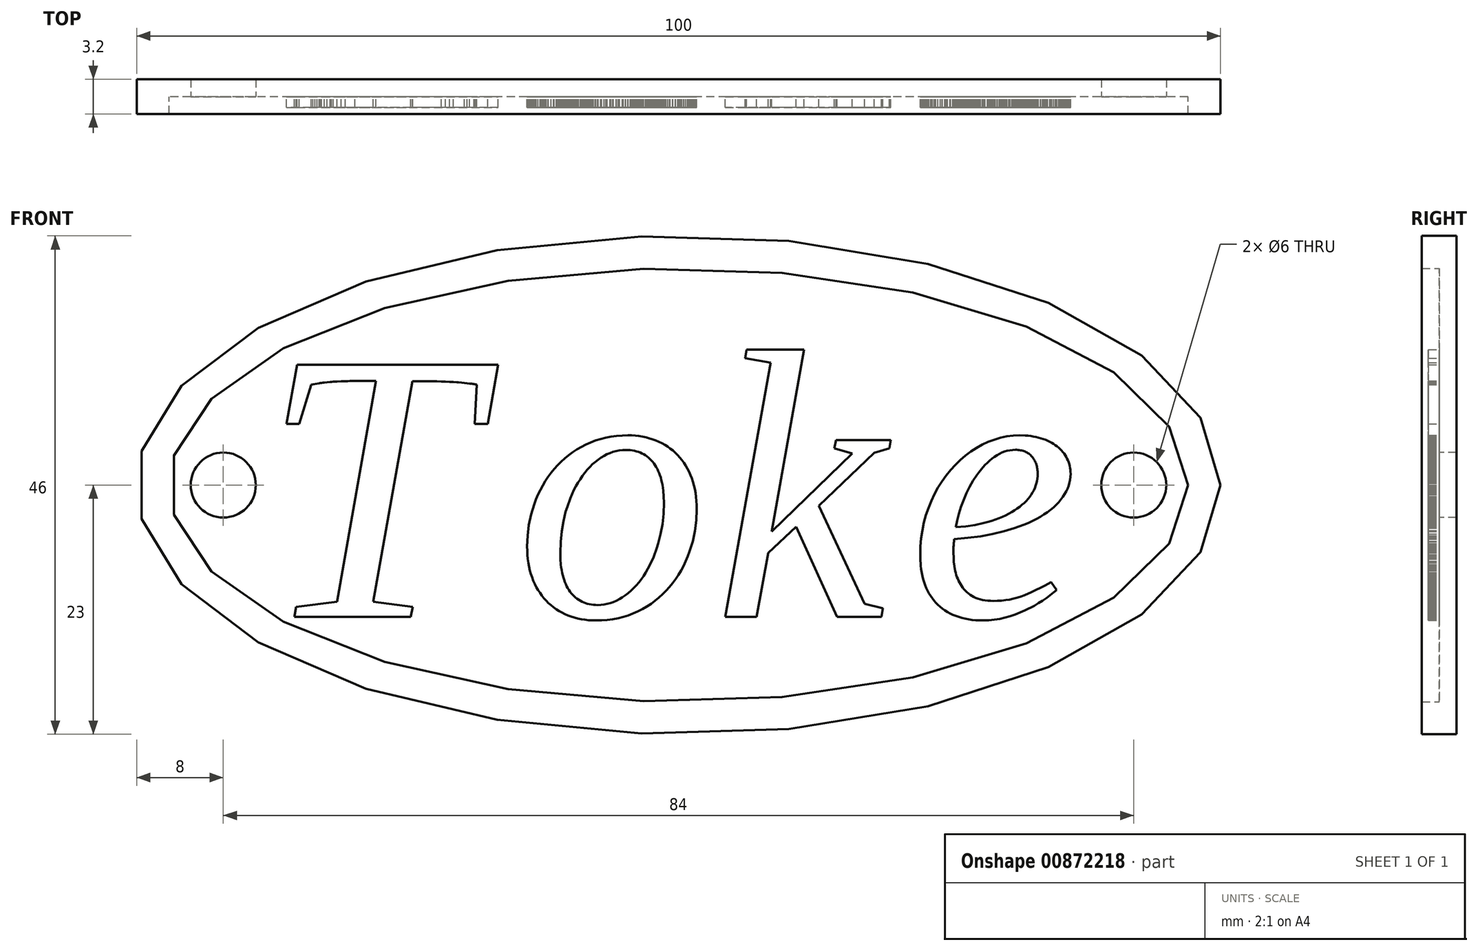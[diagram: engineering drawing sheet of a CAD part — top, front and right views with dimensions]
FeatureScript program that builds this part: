
annotation { "Feature Type Name" : "Feature", "Feature Type Description" : "" }
export const myFeature = defineFeature(function(context is Context, id is Id, definition is map)
    precondition{}
    {
        {
            var Q0;
            Q0=qCreatedBy(makeId("Front.planeOp"),FACE);
            var sketch = newSketch(context, id + "F0", { "sketchPlane" : qUnion([Q0])});
            skEllipse(sketch, "E0", {"center": v(0, 0) * mm, "majorRadius": 47 * mm, "minorRadius": 20 * mm, "majorAxis": v(1, 0)});
            skEllipse(sketch, "E1", {"center": v(0, 0) * mm, "majorRadius": 50 * mm, "minorRadius": 23 * mm, "majorAxis": v(1, 0)});
            skLineSegment(sketch, "E2", {"start": v(-81.12, 0) * mm, "end": v(85, 0) * mm, "construction": true});
            skPoint(sketch, "E2.startSnap0", {"position": v(-50, 0) * mm});
            skPoint(sketch, "E2.endSnap0", {"position": v(50, 0) * mm});
            skCircle(sketch, "E3", {"center": v(-42, 0) * mm, "radius": 3 * mm});
            skCircle(sketch, "E4", {"center": v(42, 0) * mm, "radius": 3 * mm});
            skLineSegment(sketch, "E5", {"start": v(-35.45, -12.15) * mm, "end": v(-35.27, -11.23) * mm});
            skLineSegment(sketch, "E6", {"start": v(-35.27, -11.23) * mm, "end": v(-31.5, -10.77) * mm});
            skLineSegment(sketch, "E7", {"start": v(-31.5, -10.77) * mm, "end": v(-27.92, 9.62) * mm});
            skLineSegment(sketch, "E8", {"start": v(-27.92, 9.62) * mm, "end": v(-28.8, 9.62) * mm});
            skLineSegment(sketch, "E9", {"start": v(-28.8, 9.62) * mm, "end": v(-29.35, 9.62) * mm});
            skLineSegment(sketch, "E10", {"start": v(-29.35, 9.62) * mm, "end": v(-29.85, 9.61) * mm});
            skLineSegment(sketch, "E11", {"start": v(-29.85, 9.61) * mm, "end": v(-30.32, 9.6) * mm});
            skLineSegment(sketch, "E12", {"start": v(-30.32, 9.6) * mm, "end": v(-30.54, 9.6) * mm});
            skLineSegment(sketch, "E13", {"start": v(-30.54, 9.6) * mm, "end": v(-30.74, 9.59) * mm});
            skLineSegment(sketch, "E14", {"start": v(-30.74, 9.59) * mm, "end": v(-31.14, 9.57) * mm});
            skLineSegment(sketch, "E15", {"start": v(-31.14, 9.57) * mm, "end": v(-31.5, 9.56) * mm});
            skLineSegment(sketch, "E16", {"start": v(-31.5, 9.56) * mm, "end": v(-31.84, 9.54) * mm});
            skLineSegment(sketch, "E17", {"start": v(-31.84, 9.54) * mm, "end": v(-32, 9.53) * mm});
            skLineSegment(sketch, "E18", {"start": v(-32, 9.53) * mm, "end": v(-32.15, 9.52) * mm});
            skLineSegment(sketch, "E19", {"start": v(-32.15, 9.52) * mm, "end": v(-32.43, 9.49) * mm});
            skLineSegment(sketch, "E20", {"start": v(-32.43, 9.49) * mm, "end": v(-32.7, 9.46) * mm});
            skLineSegment(sketch, "E21", {"start": v(-32.7, 9.46) * mm, "end": v(-32.82, 9.44) * mm});
            skLineSegment(sketch, "E22", {"start": v(-32.82, 9.44) * mm, "end": v(-32.94, 9.43) * mm});
            skLineSegment(sketch, "E23", {"start": v(-32.94, 9.43) * mm, "end": v(-33.05, 9.41) * mm});
            skLineSegment(sketch, "E24", {"start": v(-33.05, 9.41) * mm, "end": v(-33.16, 9.4) * mm});
            skLineSegment(sketch, "E25", {"start": v(-33.16, 9.4) * mm, "end": v(-33.36, 9.37) * mm});
            skLineSegment(sketch, "E26", {"start": v(-33.36, 9.37) * mm, "end": v(-33.55, 9.34) * mm});
            skLineSegment(sketch, "E27", {"start": v(-33.55, 9.34) * mm, "end": v(-33.73, 9.3) * mm});
            skLineSegment(sketch, "E28", {"start": v(-33.73, 9.3) * mm, "end": v(-33.9, 9.27) * mm});
            skLineSegment(sketch, "E29", {"start": v(-33.9, 9.27) * mm, "end": v(-35.01, 5.65) * mm});
            skLineSegment(sketch, "E30", {"start": v(-35.01, 5.65) * mm, "end": v(-36.17, 5.65) * mm});
            skLineSegment(sketch, "E31", {"start": v(-36.17, 5.65) * mm, "end": v(-35.2, 11.11) * mm});
            skLineSegment(sketch, "E32", {"start": v(-35.2, 11.11) * mm, "end": v(-16.64, 11.11) * mm});
            skLineSegment(sketch, "E33", {"start": v(-16.64, 11.11) * mm, "end": v(-17.61, 5.65) * mm});
            skLineSegment(sketch, "E34", {"start": v(-17.61, 5.65) * mm, "end": v(-18.8, 5.65) * mm});
            skLineSegment(sketch, "E35", {"start": v(-18.8, 5.65) * mm, "end": v(-18.62, 9.27) * mm});
            skLineSegment(sketch, "E36", {"start": v(-18.62, 9.27) * mm, "end": v(-18.7, 9.29) * mm});
            skLineSegment(sketch, "E37", {"start": v(-18.7, 9.29) * mm, "end": v(-18.78, 9.3) * mm});
            skLineSegment(sketch, "E38", {"start": v(-18.78, 9.3) * mm, "end": v(-18.87, 9.32) * mm});
            skLineSegment(sketch, "E39", {"start": v(-18.87, 9.32) * mm, "end": v(-18.96, 9.33) * mm});
            skLineSegment(sketch, "E40", {"start": v(-18.96, 9.33) * mm, "end": v(-19.06, 9.35) * mm});
            skLineSegment(sketch, "E41", {"start": v(-19.06, 9.35) * mm, "end": v(-19.16, 9.36) * mm});
            skLineSegment(sketch, "E42", {"start": v(-19.16, 9.36) * mm, "end": v(-19.27, 9.37) * mm});
            skLineSegment(sketch, "E43", {"start": v(-19.27, 9.37) * mm, "end": v(-19.5, 9.4) * mm});
            skLineSegment(sketch, "E44", {"start": v(-19.5, 9.4) * mm, "end": v(-19.75, 9.42) * mm});
            skLineSegment(sketch, "E45", {"start": v(-19.75, 9.42) * mm, "end": v(-20.02, 9.45) * mm});
            skLineSegment(sketch, "E46", {"start": v(-20.02, 9.45) * mm, "end": v(-20.3, 9.47) * mm});
            skLineSegment(sketch, "E47", {"start": v(-20.3, 9.47) * mm, "end": v(-20.46, 9.48) * mm});
            skLineSegment(sketch, "E48", {"start": v(-20.46, 9.48) * mm, "end": v(-20.78, 9.5) * mm});
            skLineSegment(sketch, "E49", {"start": v(-20.78, 9.5) * mm, "end": v(-21.12, 9.53) * mm});
            skLineSegment(sketch, "E50", {"start": v(-21.12, 9.53) * mm, "end": v(-21.5, 9.54) * mm});
            skLineSegment(sketch, "E51", {"start": v(-21.5, 9.54) * mm, "end": v(-21.89, 9.56) * mm});
            skLineSegment(sketch, "E52", {"start": v(-21.89, 9.56) * mm, "end": v(-22.3, 9.57) * mm});
            skLineSegment(sketch, "E53", {"start": v(-22.3, 9.57) * mm, "end": v(-22.75, 9.58) * mm});
            skLineSegment(sketch, "E54", {"start": v(-22.75, 9.58) * mm, "end": v(-23.22, 9.58) * mm});
            skLineSegment(sketch, "E55", {"start": v(-23.22, 9.58) * mm, "end": v(-23.72, 9.59) * mm});
            skLineSegment(sketch, "E56", {"start": v(-23.72, 9.59) * mm, "end": v(-24.57, 9.59) * mm});
            skLineSegment(sketch, "E57", {"start": v(-24.57, 9.59) * mm, "end": v(-28.16, -10.77) * mm});
            skLineSegment(sketch, "E58", {"start": v(-28.16, -10.77) * mm, "end": v(-24.53, -11.23) * mm});
            skLineSegment(sketch, "E59", {"start": v(-24.53, -11.23) * mm, "end": v(-24.7, -12.15) * mm});
            skLineSegment(sketch, "E60", {"start": v(-24.7, -12.15) * mm, "end": v(-35.45, -12.15) * mm});
            skLineSegment(sketch, "E61", {"start": v(-10.91, -6.25) * mm, "end": v(-10.9, -6.82) * mm});
            skLineSegment(sketch, "E62", {"start": v(-10.9, -6.82) * mm, "end": v(-10.86, -7.36) * mm});
            skLineSegment(sketch, "E63", {"start": v(-10.86, -7.36) * mm, "end": v(-10.82, -7.61) * mm});
            skLineSegment(sketch, "E64", {"start": v(-10.82, -7.61) * mm, "end": v(-10.79, -7.86) * mm});
            skLineSegment(sketch, "E65", {"start": v(-10.79, -7.86) * mm, "end": v(-10.74, -8.1) * mm});
            skLineSegment(sketch, "E66", {"start": v(-10.74, -8.1) * mm, "end": v(-10.69, -8.32) * mm});
            skLineSegment(sketch, "E67", {"start": v(-10.69, -8.32) * mm, "end": v(-10.63, -8.54) * mm});
            skLineSegment(sketch, "E68", {"start": v(-10.63, -8.54) * mm, "end": v(-10.56, -8.76) * mm});
            skLineSegment(sketch, "E69", {"start": v(-10.56, -8.76) * mm, "end": v(-10.49, -8.96) * mm});
            skLineSegment(sketch, "E70", {"start": v(-10.49, -8.96) * mm, "end": v(-10.4, -9.15) * mm});
            skLineSegment(sketch, "E71", {"start": v(-10.4, -9.15) * mm, "end": v(-10.32, -9.34) * mm});
            skLineSegment(sketch, "E72", {"start": v(-10.32, -9.34) * mm, "end": v(-10.22, -9.52) * mm});
            skLineSegment(sketch, "E73", {"start": v(-10.22, -9.52) * mm, "end": v(-10.12, -9.69) * mm});
            skLineSegment(sketch, "E74", {"start": v(-10.12, -9.69) * mm, "end": v(-10.01, -9.85) * mm});
            skLineSegment(sketch, "E75", {"start": v(-10.01, -9.85) * mm, "end": v(-9.9, -10) * mm});
            skLineSegment(sketch, "E76", {"start": v(-9.9, -10) * mm, "end": v(-9.77, -10.13) * mm});
            skLineSegment(sketch, "E77", {"start": v(-9.77, -10.13) * mm, "end": v(-9.64, -10.26) * mm});
            skLineSegment(sketch, "E78", {"start": v(-9.64, -10.26) * mm, "end": v(-9.5, -10.38) * mm});
            skLineSegment(sketch, "E79", {"start": v(-9.5, -10.38) * mm, "end": v(-9.37, -10.5) * mm});
            skLineSegment(sketch, "E80", {"start": v(-9.37, -10.5) * mm, "end": v(-9.22, -10.6) * mm});
            skLineSegment(sketch, "E81", {"start": v(-9.22, -10.6) * mm, "end": v(-9.07, -10.69) * mm});
            skLineSegment(sketch, "E82", {"start": v(-9.07, -10.69) * mm, "end": v(-8.91, -10.77) * mm});
            skLineSegment(sketch, "E83", {"start": v(-8.91, -10.77) * mm, "end": v(-8.75, -10.84) * mm});
            skLineSegment(sketch, "E84", {"start": v(-8.75, -10.84) * mm, "end": v(-8.58, -10.9) * mm});
            skLineSegment(sketch, "E85", {"start": v(-8.58, -10.9) * mm, "end": v(-8.41, -10.96) * mm});
            skLineSegment(sketch, "E86", {"start": v(-8.41, -10.96) * mm, "end": v(-8.23, -11) * mm});
            skLineSegment(sketch, "E87", {"start": v(-8.23, -11) * mm, "end": v(-8.05, -11.03) * mm});
            skLineSegment(sketch, "E88", {"start": v(-8.05, -11.03) * mm, "end": v(-7.86, -11.06) * mm});
            skLineSegment(sketch, "E89", {"start": v(-7.86, -11.06) * mm, "end": v(-7.66, -11.07) * mm});
            skLineSegment(sketch, "E90", {"start": v(-7.66, -11.07) * mm, "end": v(-7.46, -11.08) * mm});
            skLineSegment(sketch, "E91", {"start": v(-7.46, -11.08) * mm, "end": v(-7.16, -11.07) * mm});
            skLineSegment(sketch, "E92", {"start": v(-7.16, -11.07) * mm, "end": v(-6.87, -11.03) * mm});
            skLineSegment(sketch, "E93", {"start": v(-6.87, -11.03) * mm, "end": v(-6.58, -10.98) * mm});
            skLineSegment(sketch, "E94", {"start": v(-6.58, -10.98) * mm, "end": v(-6.29, -10.9) * mm});
            skLineSegment(sketch, "E95", {"start": v(-6.29, -10.9) * mm, "end": v(-6, -10.8) * mm});
            skLineSegment(sketch, "E96", {"start": v(-6, -10.8) * mm, "end": v(-5.72, -10.68) * mm});
            skLineSegment(sketch, "E97", {"start": v(-5.72, -10.68) * mm, "end": v(-5.45, -10.53) * mm});
            skLineSegment(sketch, "E98", {"start": v(-5.45, -10.53) * mm, "end": v(-5.17, -10.37) * mm});
            skLineSegment(sketch, "E99", {"start": v(-5.17, -10.37) * mm, "end": v(-4.9, -10.18) * mm});
            skLineSegment(sketch, "E100", {"start": v(-4.9, -10.18) * mm, "end": v(-4.63, -9.97) * mm});
            skLineSegment(sketch, "E101", {"start": v(-4.63, -9.97) * mm, "end": v(-4.38, -9.75) * mm});
            skLineSegment(sketch, "E102", {"start": v(-4.38, -9.75) * mm, "end": v(-4.13, -9.5) * mm});
            skLineSegment(sketch, "E103", {"start": v(-4.13, -9.5) * mm, "end": v(-3.9, -9.25) * mm});
            skLineSegment(sketch, "E104", {"start": v(-3.9, -9.25) * mm, "end": v(-3.66, -8.98) * mm});
            skLineSegment(sketch, "E105", {"start": v(-3.66, -8.98) * mm, "end": v(-3.44, -8.7) * mm});
            skLineSegment(sketch, "E106", {"start": v(-3.44, -8.7) * mm, "end": v(-3.23, -8.39) * mm});
            skLineSegment(sketch, "E107", {"start": v(-3.23, -8.39) * mm, "end": v(-3.02, -8.06) * mm});
            skLineSegment(sketch, "E108", {"start": v(-3.02, -8.06) * mm, "end": v(-2.82, -7.73) * mm});
            skLineSegment(sketch, "E109", {"start": v(-2.82, -7.73) * mm, "end": v(-2.64, -7.38) * mm});
            skLineSegment(sketch, "E110", {"start": v(-2.64, -7.38) * mm, "end": v(-2.3, -6.63) * mm});
            skLineSegment(sketch, "E111", {"start": v(-2.3, -6.63) * mm, "end": v(-2, -5.83) * mm});
            skLineSegment(sketch, "E112", {"start": v(-2, -5.83) * mm, "end": v(-1.87, -5.4) * mm});
            skLineSegment(sketch, "E113", {"start": v(-1.87, -5.4) * mm, "end": v(-1.65, -4.52) * mm});
            skLineSegment(sketch, "E114", {"start": v(-1.65, -4.52) * mm, "end": v(-1.48, -3.6) * mm});
            skLineSegment(sketch, "E115", {"start": v(-1.48, -3.6) * mm, "end": v(-1.39, -2.64) * mm});
            skLineSegment(sketch, "E116", {"start": v(-1.39, -2.64) * mm, "end": v(-1.35, -1.64) * mm});
            skLineSegment(sketch, "E117", {"start": v(-1.35, -1.64) * mm, "end": v(-1.37, -1.06) * mm});
            skLineSegment(sketch, "E118", {"start": v(-1.37, -1.06) * mm, "end": v(-1.41, -0.52) * mm});
            skLineSegment(sketch, "E119", {"start": v(-1.41, -0.52) * mm, "end": v(-1.44, -0.26) * mm});
            skLineSegment(sketch, "E120", {"start": v(-1.44, -0.26) * mm, "end": v(-1.48, 0) * mm});
            skLineSegment(sketch, "E121", {"start": v(-1.48, 0) * mm, "end": v(-1.53, 0.23) * mm});
            skLineSegment(sketch, "E122", {"start": v(-1.53, 0.23) * mm, "end": v(-1.58, 0.46) * mm});
            skLineSegment(sketch, "E123", {"start": v(-1.58, 0.46) * mm, "end": v(-1.64, 0.69) * mm});
            skLineSegment(sketch, "E124", {"start": v(-1.64, 0.69) * mm, "end": v(-1.71, 0.9) * mm});
            skLineSegment(sketch, "E125", {"start": v(-1.71, 0.9) * mm, "end": v(-1.79, 1.1) * mm});
            skLineSegment(sketch, "E126", {"start": v(-1.79, 1.1) * mm, "end": v(-1.87, 1.3) * mm});
            skLineSegment(sketch, "E127", {"start": v(-1.87, 1.3) * mm, "end": v(-1.96, 1.48) * mm});
            skLineSegment(sketch, "E128", {"start": v(-1.96, 1.48) * mm, "end": v(-2.06, 1.66) * mm});
            skLineSegment(sketch, "E129", {"start": v(-2.06, 1.66) * mm, "end": v(-2.16, 1.83) * mm});
            skLineSegment(sketch, "E130", {"start": v(-2.16, 1.83) * mm, "end": v(-2.27, 1.99) * mm});
            skLineSegment(sketch, "E131", {"start": v(-2.27, 1.99) * mm, "end": v(-2.39, 2.14) * mm});
            skLineSegment(sketch, "E132", {"start": v(-2.39, 2.14) * mm, "end": v(-2.51, 2.28) * mm});
            skLineSegment(sketch, "E133", {"start": v(-2.51, 2.28) * mm, "end": v(-2.64, 2.41) * mm});
            skLineSegment(sketch, "E134", {"start": v(-2.64, 2.41) * mm, "end": v(-2.77, 2.53) * mm});
            skLineSegment(sketch, "E135", {"start": v(-2.77, 2.53) * mm, "end": v(-2.91, 2.65) * mm});
            skLineSegment(sketch, "E136", {"start": v(-2.91, 2.65) * mm, "end": v(-3.06, 2.75) * mm});
            skLineSegment(sketch, "E137", {"start": v(-3.06, 2.75) * mm, "end": v(-3.22, 2.84) * mm});
            skLineSegment(sketch, "E138", {"start": v(-3.22, 2.84) * mm, "end": v(-3.37, 2.92) * mm});
            skLineSegment(sketch, "E139", {"start": v(-3.37, 2.92) * mm, "end": v(-3.54, 3) * mm});
            skLineSegment(sketch, "E140", {"start": v(-3.54, 3) * mm, "end": v(-3.71, 3.06) * mm});
            skLineSegment(sketch, "E141", {"start": v(-3.71, 3.06) * mm, "end": v(-3.9, 3.11) * mm});
            skLineSegment(sketch, "E142", {"start": v(-3.9, 3.11) * mm, "end": v(-4.08, 3.16) * mm});
            skLineSegment(sketch, "E143", {"start": v(-4.08, 3.16) * mm, "end": v(-4.27, 3.2) * mm});
            skLineSegment(sketch, "E144", {"start": v(-4.27, 3.2) * mm, "end": v(-4.46, 3.22) * mm});
            skLineSegment(sketch, "E145", {"start": v(-4.46, 3.22) * mm, "end": v(-4.67, 3.23) * mm});
            skLineSegment(sketch, "E146", {"start": v(-4.67, 3.23) * mm, "end": v(-4.88, 3.24) * mm});
            skLineSegment(sketch, "E147", {"start": v(-4.88, 3.24) * mm, "end": v(-5.17, 3.22) * mm});
            skLineSegment(sketch, "E148", {"start": v(-5.17, 3.22) * mm, "end": v(-5.46, 3.2) * mm});
            skLineSegment(sketch, "E149", {"start": v(-5.46, 3.2) * mm, "end": v(-5.75, 3.14) * mm});
            skLineSegment(sketch, "E150", {"start": v(-5.75, 3.14) * mm, "end": v(-6.03, 3.06) * mm});
            skLineSegment(sketch, "E151", {"start": v(-6.03, 3.06) * mm, "end": v(-6.32, 2.96) * mm});
            skLineSegment(sketch, "E152", {"start": v(-6.32, 2.96) * mm, "end": v(-6.6, 2.84) * mm});
            skLineSegment(sketch, "E153", {"start": v(-6.6, 2.84) * mm, "end": v(-6.87, 2.7) * mm});
            skLineSegment(sketch, "E154", {"start": v(-6.87, 2.7) * mm, "end": v(-7.15, 2.52) * mm});
            skLineSegment(sketch, "E155", {"start": v(-7.15, 2.52) * mm, "end": v(-7.42, 2.34) * mm});
            skLineSegment(sketch, "E156", {"start": v(-7.42, 2.34) * mm, "end": v(-7.68, 2.13) * mm});
            skLineSegment(sketch, "E157", {"start": v(-7.68, 2.13) * mm, "end": v(-7.93, 1.91) * mm});
            skLineSegment(sketch, "E158", {"start": v(-7.93, 1.91) * mm, "end": v(-8.18, 1.67) * mm});
            skLineSegment(sketch, "E159", {"start": v(-8.18, 1.67) * mm, "end": v(-8.41, 1.42) * mm});
            skLineSegment(sketch, "E160", {"start": v(-8.41, 1.42) * mm, "end": v(-8.64, 1.15) * mm});
            skLineSegment(sketch, "E161", {"start": v(-8.64, 1.15) * mm, "end": v(-8.86, 0.85) * mm});
            skLineSegment(sketch, "E162", {"start": v(-8.86, 0.85) * mm, "end": v(-9.07, 0.55) * mm});
            skLineSegment(sketch, "E163", {"start": v(-9.07, 0.55) * mm, "end": v(-9.28, 0.23) * mm});
            skLineSegment(sketch, "E164", {"start": v(-9.28, 0.23) * mm, "end": v(-9.47, -0.1) * mm});
            skLineSegment(sketch, "E165", {"start": v(-9.47, -0.1) * mm, "end": v(-9.65, -0.46) * mm});
            skLineSegment(sketch, "E166", {"start": v(-9.65, -0.46) * mm, "end": v(-9.82, -0.83) * mm});
            skLineSegment(sketch, "E167", {"start": v(-9.82, -0.83) * mm, "end": v(-9.99, -1.21) * mm});
            skLineSegment(sketch, "E168", {"start": v(-9.99, -1.21) * mm, "end": v(-10.28, -2.02) * mm});
            skLineSegment(sketch, "E169", {"start": v(-10.28, -2.02) * mm, "end": v(-10.4, -2.45) * mm});
            skLineSegment(sketch, "E170", {"start": v(-10.4, -2.45) * mm, "end": v(-10.63, -3.34) * mm});
            skLineSegment(sketch, "E171", {"start": v(-10.63, -3.34) * mm, "end": v(-10.79, -4.27) * mm});
            skLineSegment(sketch, "E172", {"start": v(-10.79, -4.27) * mm, "end": v(-10.88, -5.24) * mm});
            skLineSegment(sketch, "E173", {"start": v(-10.88, -5.24) * mm, "end": v(-10.91, -6.25) * mm});
            skLineSegment(sketch, "E174", {"start": v(-7.62, -12.5) * mm, "end": v(-7.96, -12.5) * mm});
            skLineSegment(sketch, "E175", {"start": v(-7.96, -12.5) * mm, "end": v(-8.3, -12.47) * mm});
            skLineSegment(sketch, "E176", {"start": v(-8.3, -12.47) * mm, "end": v(-8.64, -12.43) * mm});
            skLineSegment(sketch, "E177", {"start": v(-8.64, -12.43) * mm, "end": v(-8.97, -12.38) * mm});
            skLineSegment(sketch, "E178", {"start": v(-8.97, -12.38) * mm, "end": v(-9.29, -12.32) * mm});
            skLineSegment(sketch, "E179", {"start": v(-9.29, -12.32) * mm, "end": v(-9.6, -12.24) * mm});
            skLineSegment(sketch, "E180", {"start": v(-9.6, -12.24) * mm, "end": v(-9.9, -12.14) * mm});
            skLineSegment(sketch, "E181", {"start": v(-9.9, -12.14) * mm, "end": v(-10.2, -12.03) * mm});
            skLineSegment(sketch, "E182", {"start": v(-10.2, -12.03) * mm, "end": v(-10.49, -11.9) * mm});
            skLineSegment(sketch, "E183", {"start": v(-10.49, -11.9) * mm, "end": v(-10.76, -11.77) * mm});
            skLineSegment(sketch, "E184", {"start": v(-10.76, -11.77) * mm, "end": v(-11.03, -11.62) * mm});
            skLineSegment(sketch, "E185", {"start": v(-11.03, -11.62) * mm, "end": v(-11.29, -11.46) * mm});
            skLineSegment(sketch, "E186", {"start": v(-11.29, -11.46) * mm, "end": v(-11.53, -11.28) * mm});
            skLineSegment(sketch, "E187", {"start": v(-11.53, -11.28) * mm, "end": v(-11.77, -11.1) * mm});
            skLineSegment(sketch, "E188", {"start": v(-11.77, -11.1) * mm, "end": v(-12, -10.9) * mm});
            skLineSegment(sketch, "E189", {"start": v(-12, -10.9) * mm, "end": v(-12.21, -10.68) * mm});
            skLineSegment(sketch, "E190", {"start": v(-12.21, -10.68) * mm, "end": v(-12.42, -10.45) * mm});
            skLineSegment(sketch, "E191", {"start": v(-12.42, -10.45) * mm, "end": v(-12.6, -10.21) * mm});
            skLineSegment(sketch, "E192", {"start": v(-12.6, -10.21) * mm, "end": v(-12.79, -9.96) * mm});
            skLineSegment(sketch, "E193", {"start": v(-12.79, -9.96) * mm, "end": v(-12.96, -9.7) * mm});
            skLineSegment(sketch, "E194", {"start": v(-12.96, -9.7) * mm, "end": v(-13.11, -9.42) * mm});
            skLineSegment(sketch, "E195", {"start": v(-13.11, -9.42) * mm, "end": v(-13.26, -9.14) * mm});
            skLineSegment(sketch, "E196", {"start": v(-13.26, -9.14) * mm, "end": v(-13.4, -8.84) * mm});
            skLineSegment(sketch, "E197", {"start": v(-13.4, -8.84) * mm, "end": v(-13.52, -8.53) * mm});
            skLineSegment(sketch, "E198", {"start": v(-13.52, -8.53) * mm, "end": v(-13.62, -8.2) * mm});
            skLineSegment(sketch, "E199", {"start": v(-13.62, -8.2) * mm, "end": v(-13.71, -7.87) * mm});
            skLineSegment(sketch, "E200", {"start": v(-13.71, -7.87) * mm, "end": v(-13.8, -7.53) * mm});
            skLineSegment(sketch, "E201", {"start": v(-13.8, -7.53) * mm, "end": v(-13.85, -7.18) * mm});
            skLineSegment(sketch, "E202", {"start": v(-13.85, -7.18) * mm, "end": v(-13.9, -6.82) * mm});
            skLineSegment(sketch, "E203", {"start": v(-13.9, -6.82) * mm, "end": v(-13.94, -6.44) * mm});
            skLineSegment(sketch, "E204", {"start": v(-13.94, -6.44) * mm, "end": v(-13.96, -6.06) * mm});
            skLineSegment(sketch, "E205", {"start": v(-13.96, -6.06) * mm, "end": v(-13.97, -5.66) * mm});
            skLineSegment(sketch, "E206", {"start": v(-13.97, -5.66) * mm, "end": v(-13.93, -4.66) * mm});
            skLineSegment(sketch, "E207", {"start": v(-13.93, -4.66) * mm, "end": v(-13.8, -3.68) * mm});
            skLineSegment(sketch, "E208", {"start": v(-13.8, -3.68) * mm, "end": v(-13.6, -2.72) * mm});
            skLineSegment(sketch, "E209", {"start": v(-13.6, -2.72) * mm, "end": v(-13.32, -1.78) * mm});
            skLineSegment(sketch, "E210", {"start": v(-13.32, -1.78) * mm, "end": v(-13.15, -1.32) * mm});
            skLineSegment(sketch, "E211", {"start": v(-13.15, -1.32) * mm, "end": v(-12.96, -0.88) * mm});
            skLineSegment(sketch, "E212", {"start": v(-12.96, -0.88) * mm, "end": v(-12.75, -0.45) * mm});
            skLineSegment(sketch, "E213", {"start": v(-12.75, -0.45) * mm, "end": v(-12.53, -0.03) * mm});
            skLineSegment(sketch, "E214", {"start": v(-12.53, -0.03) * mm, "end": v(-12.3, 0.37) * mm});
            skLineSegment(sketch, "E215", {"start": v(-12.3, 0.37) * mm, "end": v(-12.03, 0.75) * mm});
            skLineSegment(sketch, "E216", {"start": v(-12.03, 0.75) * mm, "end": v(-11.76, 1.13) * mm});
            skLineSegment(sketch, "E217", {"start": v(-11.76, 1.13) * mm, "end": v(-11.47, 1.48) * mm});
            skLineSegment(sketch, "E218", {"start": v(-11.47, 1.48) * mm, "end": v(-11.16, 1.83) * mm});
            skLineSegment(sketch, "E219", {"start": v(-11.16, 1.83) * mm, "end": v(-10.83, 2.16) * mm});
            skLineSegment(sketch, "E220", {"start": v(-10.83, 2.16) * mm, "end": v(-10.49, 2.47) * mm});
            skLineSegment(sketch, "E221", {"start": v(-10.49, 2.47) * mm, "end": v(-10.13, 2.76) * mm});
            skLineSegment(sketch, "E222", {"start": v(-10.13, 2.76) * mm, "end": v(-9.75, 3.03) * mm});
            skLineSegment(sketch, "E223", {"start": v(-9.75, 3.03) * mm, "end": v(-9.36, 3.29) * mm});
            skLineSegment(sketch, "E224", {"start": v(-9.36, 3.29) * mm, "end": v(-8.96, 3.52) * mm});
            skLineSegment(sketch, "E225", {"start": v(-8.96, 3.52) * mm, "end": v(-8.54, 3.74) * mm});
            skLineSegment(sketch, "E226", {"start": v(-8.54, 3.74) * mm, "end": v(-8.1, 3.94) * mm});
            skLineSegment(sketch, "E227", {"start": v(-8.1, 3.94) * mm, "end": v(-7.65, 4.11) * mm});
            skLineSegment(sketch, "E228", {"start": v(-7.65, 4.11) * mm, "end": v(-7.19, 4.26) * mm});
            skLineSegment(sketch, "E229", {"start": v(-7.19, 4.26) * mm, "end": v(-6.71, 4.38) * mm});
            skLineSegment(sketch, "E230", {"start": v(-6.71, 4.38) * mm, "end": v(-6.22, 4.47) * mm});
            skLineSegment(sketch, "E231", {"start": v(-6.22, 4.47) * mm, "end": v(-5.72, 4.54) * mm});
            skLineSegment(sketch, "E232", {"start": v(-5.72, 4.54) * mm, "end": v(-5.2, 4.58) * mm});
            skLineSegment(sketch, "E233", {"start": v(-5.2, 4.58) * mm, "end": v(-4.67, 4.59) * mm});
            skLineSegment(sketch, "E234", {"start": v(-4.67, 4.59) * mm, "end": v(-4.32, 4.58) * mm});
            skLineSegment(sketch, "E235", {"start": v(-4.32, 4.58) * mm, "end": v(-3.98, 4.56) * mm});
            skLineSegment(sketch, "E236", {"start": v(-3.98, 4.56) * mm, "end": v(-3.65, 4.52) * mm});
            skLineSegment(sketch, "E237", {"start": v(-3.65, 4.52) * mm, "end": v(-3.32, 4.47) * mm});
            skLineSegment(sketch, "E238", {"start": v(-3.32, 4.47) * mm, "end": v(-3, 4.4) * mm});
            skLineSegment(sketch, "E239", {"start": v(-3, 4.4) * mm, "end": v(-2.7, 4.33) * mm});
            skLineSegment(sketch, "E240", {"start": v(-2.7, 4.33) * mm, "end": v(-2.4, 4.23) * mm});
            skLineSegment(sketch, "E241", {"start": v(-2.4, 4.23) * mm, "end": v(-2.1, 4.12) * mm});
            skLineSegment(sketch, "E242", {"start": v(-2.1, 4.12) * mm, "end": v(-1.81, 4) * mm});
            skLineSegment(sketch, "E243", {"start": v(-1.81, 4) * mm, "end": v(-1.53, 3.86) * mm});
            skLineSegment(sketch, "E244", {"start": v(-1.53, 3.86) * mm, "end": v(-1.26, 3.71) * mm});
            skLineSegment(sketch, "E245", {"start": v(-1.26, 3.71) * mm, "end": v(-1, 3.55) * mm});
            skLineSegment(sketch, "E246", {"start": v(-1, 3.55) * mm, "end": v(-0.76, 3.37) * mm});
            skLineSegment(sketch, "E247", {"start": v(-0.76, 3.37) * mm, "end": v(-0.53, 3.18) * mm});
            skLineSegment(sketch, "E248", {"start": v(-0.53, 3.18) * mm, "end": v(-0.3, 2.98) * mm});
            skLineSegment(sketch, "E249", {"start": v(-0.3, 2.98) * mm, "end": v(-0.09, 2.77) * mm});
            skLineSegment(sketch, "E250", {"start": v(-0.09, 2.77) * mm, "end": v(0.12, 2.54) * mm});
            skLineSegment(sketch, "E251", {"start": v(0.12, 2.54) * mm, "end": v(0.31, 2.3) * mm});
            skLineSegment(sketch, "E252", {"start": v(0.31, 2.3) * mm, "end": v(0.5, 2.05) * mm});
            skLineSegment(sketch, "E253", {"start": v(0.5, 2.05) * mm, "end": v(0.66, 1.79) * mm});
            skLineSegment(sketch, "E254", {"start": v(0.66, 1.79) * mm, "end": v(0.82, 1.51) * mm});
            skLineSegment(sketch, "E255", {"start": v(0.82, 1.51) * mm, "end": v(0.96, 1.23) * mm});
            skLineSegment(sketch, "E256", {"start": v(0.96, 1.23) * mm, "end": v(1.1, 0.93) * mm});
            skLineSegment(sketch, "E257", {"start": v(1.1, 0.93) * mm, "end": v(1.21, 0.62) * mm});
            skLineSegment(sketch, "E258", {"start": v(1.21, 0.62) * mm, "end": v(1.32, 0.3) * mm});
            skLineSegment(sketch, "E259", {"start": v(1.32, 0.3) * mm, "end": v(1.42, -0.04) * mm});
            skLineSegment(sketch, "E260", {"start": v(1.42, -0.04) * mm, "end": v(1.5, -0.38) * mm});
            skLineSegment(sketch, "E261", {"start": v(1.5, -0.38) * mm, "end": v(1.57, -0.73) * mm});
            skLineSegment(sketch, "E262", {"start": v(1.57, -0.73) * mm, "end": v(1.62, -1.1) * mm});
            skLineSegment(sketch, "E263", {"start": v(1.62, -1.1) * mm, "end": v(1.65, -1.47) * mm});
            skLineSegment(sketch, "E264", {"start": v(1.65, -1.47) * mm, "end": v(1.68, -1.85) * mm});
            skLineSegment(sketch, "E265", {"start": v(1.68, -1.85) * mm, "end": v(1.68, -2.25) * mm});
            skLineSegment(sketch, "E266", {"start": v(1.68, -2.25) * mm, "end": v(1.64, -3.25) * mm});
            skLineSegment(sketch, "E267", {"start": v(1.64, -3.25) * mm, "end": v(1.52, -4.23) * mm});
            skLineSegment(sketch, "E268", {"start": v(1.52, -4.23) * mm, "end": v(1.31, -5.2) * mm});
            skLineSegment(sketch, "E269", {"start": v(1.31, -5.2) * mm, "end": v(1.02, -6.13) * mm});
            skLineSegment(sketch, "E270", {"start": v(1.02, -6.13) * mm, "end": v(0.85, -6.6) * mm});
            skLineSegment(sketch, "E271", {"start": v(0.85, -6.6) * mm, "end": v(0.67, -7.03) * mm});
            skLineSegment(sketch, "E272", {"start": v(0.67, -7.03) * mm, "end": v(0.46, -7.46) * mm});
            skLineSegment(sketch, "E273", {"start": v(0.46, -7.46) * mm, "end": v(0.24, -7.88) * mm});
            skLineSegment(sketch, "E274", {"start": v(0.24, -7.88) * mm, "end": v(0, -8.28) * mm});
            skLineSegment(sketch, "E275", {"start": v(0, -8.28) * mm, "end": v(-0.26, -8.67) * mm});
            skLineSegment(sketch, "E276", {"start": v(-0.26, -8.67) * mm, "end": v(-0.54, -9.05) * mm});
            skLineSegment(sketch, "E277", {"start": v(-0.54, -9.05) * mm, "end": v(-0.83, -9.41) * mm});
            skLineSegment(sketch, "E278", {"start": v(-0.83, -9.41) * mm, "end": v(-1.14, -9.75) * mm});
            skLineSegment(sketch, "E279", {"start": v(-1.14, -9.75) * mm, "end": v(-1.46, -10.08) * mm});
            skLineSegment(sketch, "E280", {"start": v(-1.46, -10.08) * mm, "end": v(-1.8, -10.39) * mm});
            skLineSegment(sketch, "E281", {"start": v(-1.8, -10.39) * mm, "end": v(-2.16, -10.68) * mm});
            skLineSegment(sketch, "E282", {"start": v(-2.16, -10.68) * mm, "end": v(-2.53, -10.95) * mm});
            skLineSegment(sketch, "E283", {"start": v(-2.53, -10.95) * mm, "end": v(-2.92, -11.2) * mm});
            skLineSegment(sketch, "E284", {"start": v(-2.92, -11.2) * mm, "end": v(-3.33, -11.45) * mm});
            skLineSegment(sketch, "E285", {"start": v(-3.33, -11.45) * mm, "end": v(-3.75, -11.67) * mm});
            skLineSegment(sketch, "E286", {"start": v(-3.75, -11.67) * mm, "end": v(-4.18, -11.86) * mm});
            skLineSegment(sketch, "E287", {"start": v(-4.18, -11.86) * mm, "end": v(-4.63, -12.03) * mm});
            skLineSegment(sketch, "E288", {"start": v(-4.63, -12.03) * mm, "end": v(-5.1, -12.17) * mm});
            skLineSegment(sketch, "E289", {"start": v(-5.1, -12.17) * mm, "end": v(-5.57, -12.3) * mm});
            skLineSegment(sketch, "E290", {"start": v(-5.57, -12.3) * mm, "end": v(-6.06, -12.38) * mm});
            skLineSegment(sketch, "E291", {"start": v(-6.06, -12.38) * mm, "end": v(-6.57, -12.45) * mm});
            skLineSegment(sketch, "E292", {"start": v(-6.57, -12.45) * mm, "end": v(-7.09, -12.49) * mm});
            skLineSegment(sketch, "E293", {"start": v(-7.09, -12.49) * mm, "end": v(-7.62, -12.5) * mm});
            skLineSegment(sketch, "E294", {"start": v(8.48, 11.3) * mm, "end": v(6.14, 11.72) * mm});
            skLineSegment(sketch, "E295", {"start": v(6.14, 11.72) * mm, "end": v(6.28, 12.5) * mm});
            skLineSegment(sketch, "E296", {"start": v(6.28, 12.5) * mm, "end": v(11.57, 12.5) * mm});
            skLineSegment(sketch, "E297", {"start": v(11.57, 12.5) * mm, "end": v(8.59, -4.3) * mm});
            skLineSegment(sketch, "E298", {"start": v(8.59, -4.3) * mm, "end": v(16.01, 2.9) * mm});
            skLineSegment(sketch, "E299", {"start": v(16.01, 2.9) * mm, "end": v(14.38, 3.37) * mm});
            skLineSegment(sketch, "E300", {"start": v(14.38, 3.37) * mm, "end": v(14.52, 4.16) * mm});
            skLineSegment(sketch, "E301", {"start": v(14.52, 4.16) * mm, "end": v(19.59, 4.16) * mm});
            skLineSegment(sketch, "E302", {"start": v(19.59, 4.16) * mm, "end": v(19.45, 3.37) * mm});
            skLineSegment(sketch, "E303", {"start": v(19.45, 3.37) * mm, "end": v(18.04, 2.98) * mm});
            skLineSegment(sketch, "E304", {"start": v(18.04, 2.98) * mm, "end": v(12.94, -1.9) * mm});
            skLineSegment(sketch, "E305", {"start": v(12.94, -1.9) * mm, "end": v(17.16, -10.97) * mm});
            skLineSegment(sketch, "E306", {"start": v(17.16, -10.97) * mm, "end": v(18.86, -11.37) * mm});
            skLineSegment(sketch, "E307", {"start": v(18.86, -11.37) * mm, "end": v(18.72, -12.15) * mm});
            skLineSegment(sketch, "E308", {"start": v(18.72, -12.15) * mm, "end": v(14.63, -12.15) * mm});
            skLineSegment(sketch, "E309", {"start": v(14.63, -12.15) * mm, "end": v(10.84, -3.84) * mm});
            skLineSegment(sketch, "E310", {"start": v(10.84, -3.84) * mm, "end": v(8.28, -6.25) * mm});
            skLineSegment(sketch, "E311", {"start": v(8.28, -6.25) * mm, "end": v(7.2, -12.15) * mm});
            skLineSegment(sketch, "E312", {"start": v(7.2, -12.15) * mm, "end": v(4.32, -12.15) * mm});
            skLineSegment(sketch, "E313", {"start": v(4.32, -12.15) * mm, "end": v(8.48, 11.3) * mm});
            skLineSegment(sketch, "E314", {"start": v(36.17, 1.03) * mm, "end": v(36.16, 0.75) * mm});
            skLineSegment(sketch, "E315", {"start": v(36.16, 0.75) * mm, "end": v(36.13, 0.48) * mm});
            skLineSegment(sketch, "E316", {"start": v(36.13, 0.48) * mm, "end": v(36.07, 0.2) * mm});
            skLineSegment(sketch, "E317", {"start": v(36.07, 0.2) * mm, "end": v(36, -0.07) * mm});
            skLineSegment(sketch, "E318", {"start": v(36, -0.07) * mm, "end": v(35.9, -0.33) * mm});
            skLineSegment(sketch, "E319", {"start": v(35.9, -0.33) * mm, "end": v(35.77, -0.6) * mm});
            skLineSegment(sketch, "E320", {"start": v(35.77, -0.6) * mm, "end": v(35.63, -0.85) * mm});
            skLineSegment(sketch, "E321", {"start": v(35.63, -0.85) * mm, "end": v(35.46, -1.1) * mm});
            skLineSegment(sketch, "E322", {"start": v(35.46, -1.1) * mm, "end": v(35.27, -1.35) * mm});
            skLineSegment(sketch, "E323", {"start": v(35.27, -1.35) * mm, "end": v(35.07, -1.6) * mm});
            skLineSegment(sketch, "E324", {"start": v(35.07, -1.6) * mm, "end": v(34.84, -1.83) * mm});
            skLineSegment(sketch, "E325", {"start": v(34.84, -1.83) * mm, "end": v(34.59, -2.06) * mm});
            skLineSegment(sketch, "E326", {"start": v(34.59, -2.06) * mm, "end": v(34.32, -2.28) * mm});
            skLineSegment(sketch, "E327", {"start": v(34.32, -2.28) * mm, "end": v(34.02, -2.5) * mm});
            skLineSegment(sketch, "E328", {"start": v(34.02, -2.5) * mm, "end": v(33.71, -2.72) * mm});
            skLineSegment(sketch, "E329", {"start": v(33.71, -2.72) * mm, "end": v(33.38, -2.92) * mm});
            skLineSegment(sketch, "E330", {"start": v(33.38, -2.92) * mm, "end": v(33.03, -3.12) * mm});
            skLineSegment(sketch, "E331", {"start": v(33.03, -3.12) * mm, "end": v(32.66, -3.3) * mm});
            skLineSegment(sketch, "E332", {"start": v(32.66, -3.3) * mm, "end": v(32.27, -3.49) * mm});
            skLineSegment(sketch, "E333", {"start": v(32.27, -3.49) * mm, "end": v(31.86, -3.66) * mm});
            skLineSegment(sketch, "E334", {"start": v(31.86, -3.66) * mm, "end": v(31.43, -3.83) * mm});
            skLineSegment(sketch, "E335", {"start": v(31.43, -3.83) * mm, "end": v(30.98, -3.98) * mm});
            skLineSegment(sketch, "E336", {"start": v(30.98, -3.98) * mm, "end": v(30.02, -4.28) * mm});
            skLineSegment(sketch, "E337", {"start": v(30.02, -4.28) * mm, "end": v(28.98, -4.52) * mm});
            skLineSegment(sketch, "E338", {"start": v(28.98, -4.52) * mm, "end": v(27.87, -4.72) * mm});
            skLineSegment(sketch, "E339", {"start": v(27.87, -4.72) * mm, "end": v(26.7, -4.88) * mm});
            skLineSegment(sketch, "E340", {"start": v(26.7, -4.88) * mm, "end": v(25.44, -4.99) * mm});
            skLineSegment(sketch, "E341", {"start": v(25.44, -4.99) * mm, "end": v(25.43, -5) * mm});
            skLineSegment(sketch, "E342", {"start": v(25.43, -5) * mm, "end": v(25.43, -5.03) * mm});
            skLineSegment(sketch, "E343", {"start": v(25.43, -5.03) * mm, "end": v(25.43, -5.05) * mm});
            skLineSegment(sketch, "E344", {"start": v(25.43, -5.05) * mm, "end": v(25.43, -5.08) * mm});
            skLineSegment(sketch, "E345", {"start": v(25.43, -5.08) * mm, "end": v(25.42, -5.1) * mm});
            skLineSegment(sketch, "E346", {"start": v(25.42, -5.1) * mm, "end": v(25.42, -5.13) * mm});
            skLineSegment(sketch, "E347", {"start": v(25.42, -5.13) * mm, "end": v(25.42, -5.16) * mm});
            skLineSegment(sketch, "E348", {"start": v(25.42, -5.16) * mm, "end": v(25.41, -5.19) * mm});
            skLineSegment(sketch, "E349", {"start": v(25.41, -5.19) * mm, "end": v(25.4, -5.25) * mm});
            skLineSegment(sketch, "E350", {"start": v(25.4, -5.25) * mm, "end": v(25.4, -5.32) * mm});
            skLineSegment(sketch, "E351", {"start": v(25.4, -5.32) * mm, "end": v(25.4, -5.4) * mm});
            skLineSegment(sketch, "E352", {"start": v(25.4, -5.4) * mm, "end": v(25.38, -5.47) * mm});
            skLineSegment(sketch, "E353", {"start": v(25.38, -5.47) * mm, "end": v(25.38, -5.56) * mm});
            skLineSegment(sketch, "E354", {"start": v(25.38, -5.56) * mm, "end": v(25.37, -5.74) * mm});
            skLineSegment(sketch, "E355", {"start": v(25.37, -5.74) * mm, "end": v(25.37, -5.93) * mm});
            skLineSegment(sketch, "E356", {"start": v(25.37, -5.93) * mm, "end": v(25.37, -6.14) * mm});
            skLineSegment(sketch, "E357", {"start": v(25.37, -6.14) * mm, "end": v(25.37, -6.25) * mm});
            skLineSegment(sketch, "E358", {"start": v(25.37, -6.25) * mm, "end": v(25.38, -6.68) * mm});
            skLineSegment(sketch, "E359", {"start": v(25.38, -6.68) * mm, "end": v(25.4, -7.1) * mm});
            skLineSegment(sketch, "E360", {"start": v(25.4, -7.1) * mm, "end": v(25.45, -7.5) * mm});
            skLineSegment(sketch, "E361", {"start": v(25.45, -7.5) * mm, "end": v(25.52, -7.9) * mm});
            skLineSegment(sketch, "E362", {"start": v(25.52, -7.9) * mm, "end": v(25.57, -8.1) * mm});
            skLineSegment(sketch, "E363", {"start": v(25.57, -8.1) * mm, "end": v(25.62, -8.3) * mm});
            skLineSegment(sketch, "E364", {"start": v(25.62, -8.3) * mm, "end": v(25.69, -8.48) * mm});
            skLineSegment(sketch, "E365", {"start": v(25.69, -8.48) * mm, "end": v(25.76, -8.66) * mm});
            skLineSegment(sketch, "E366", {"start": v(25.76, -8.66) * mm, "end": v(25.83, -8.83) * mm});
            skLineSegment(sketch, "E367", {"start": v(25.83, -8.83) * mm, "end": v(25.92, -9) * mm});
            skLineSegment(sketch, "E368", {"start": v(25.92, -9) * mm, "end": v(26.01, -9.17) * mm});
            skLineSegment(sketch, "E369", {"start": v(26.01, -9.17) * mm, "end": v(26.11, -9.33) * mm});
            skLineSegment(sketch, "E370", {"start": v(26.11, -9.33) * mm, "end": v(26.22, -9.48) * mm});
            skLineSegment(sketch, "E371", {"start": v(26.22, -9.48) * mm, "end": v(26.34, -9.62) * mm});
            skLineSegment(sketch, "E372", {"start": v(26.34, -9.62) * mm, "end": v(26.47, -9.76) * mm});
            skLineSegment(sketch, "E373", {"start": v(26.47, -9.76) * mm, "end": v(26.6, -9.89) * mm});
            skLineSegment(sketch, "E374", {"start": v(26.6, -9.89) * mm, "end": v(26.75, -10.01) * mm});
            skLineSegment(sketch, "E375", {"start": v(26.75, -10.01) * mm, "end": v(26.9, -10.13) * mm});
            skLineSegment(sketch, "E376", {"start": v(26.9, -10.13) * mm, "end": v(27.07, -10.23) * mm});
            skLineSegment(sketch, "E377", {"start": v(27.07, -10.23) * mm, "end": v(27.24, -10.33) * mm});
            skLineSegment(sketch, "E378", {"start": v(27.24, -10.33) * mm, "end": v(27.42, -10.42) * mm});
            skLineSegment(sketch, "E379", {"start": v(27.42, -10.42) * mm, "end": v(27.62, -10.5) * mm});
            skLineSegment(sketch, "E380", {"start": v(27.62, -10.5) * mm, "end": v(27.83, -10.55) * mm});
            skLineSegment(sketch, "E381", {"start": v(27.83, -10.55) * mm, "end": v(28.05, -10.6) * mm});
            skLineSegment(sketch, "E382", {"start": v(28.05, -10.6) * mm, "end": v(28.28, -10.64) * mm});
            skLineSegment(sketch, "E383", {"start": v(28.28, -10.64) * mm, "end": v(28.52, -10.67) * mm});
            skLineSegment(sketch, "E384", {"start": v(28.52, -10.67) * mm, "end": v(28.78, -10.7) * mm});
            skLineSegment(sketch, "E385", {"start": v(28.78, -10.7) * mm, "end": v(29.04, -10.7) * mm});
            skLineSegment(sketch, "E386", {"start": v(29.04, -10.7) * mm, "end": v(29.43, -10.69) * mm});
            skLineSegment(sketch, "E387", {"start": v(29.43, -10.69) * mm, "end": v(29.8, -10.66) * mm});
            skLineSegment(sketch, "E388", {"start": v(29.8, -10.66) * mm, "end": v(30.18, -10.62) * mm});
            skLineSegment(sketch, "E389", {"start": v(30.18, -10.62) * mm, "end": v(30.54, -10.57) * mm});
            skLineSegment(sketch, "E390", {"start": v(30.54, -10.57) * mm, "end": v(30.9, -10.5) * mm});
            skLineSegment(sketch, "E391", {"start": v(30.9, -10.5) * mm, "end": v(31.25, -10.4) * mm});
            skLineSegment(sketch, "E392", {"start": v(31.25, -10.4) * mm, "end": v(31.6, -10.3) * mm});
            skLineSegment(sketch, "E393", {"start": v(31.6, -10.3) * mm, "end": v(31.92, -10.18) * mm});
            skLineSegment(sketch, "E394", {"start": v(31.92, -10.18) * mm, "end": v(32.57, -9.9) * mm});
            skLineSegment(sketch, "E395", {"start": v(32.57, -9.9) * mm, "end": v(33.8, -9.3) * mm});
            skLineSegment(sketch, "E396", {"start": v(33.8, -9.3) * mm, "end": v(34.39, -8.96) * mm});
            skLineSegment(sketch, "E397", {"start": v(34.39, -8.96) * mm, "end": v(34.9, -9.69) * mm});
            skLineSegment(sketch, "E398", {"start": v(34.9, -9.69) * mm, "end": v(34.6, -9.93) * mm});
            skLineSegment(sketch, "E399", {"start": v(34.6, -9.93) * mm, "end": v(34.29, -10.17) * mm});
            skLineSegment(sketch, "E400", {"start": v(34.29, -10.17) * mm, "end": v(33.95, -10.41) * mm});
            skLineSegment(sketch, "E401", {"start": v(33.95, -10.41) * mm, "end": v(33.59, -10.66) * mm});
            skLineSegment(sketch, "E402", {"start": v(33.59, -10.66) * mm, "end": v(33.2, -10.9) * mm});
            skLineSegment(sketch, "E403", {"start": v(33.2, -10.9) * mm, "end": v(32.8, -11.14) * mm});
            skLineSegment(sketch, "E404", {"start": v(32.8, -11.14) * mm, "end": v(31.96, -11.58) * mm});
            skLineSegment(sketch, "E405", {"start": v(31.96, -11.58) * mm, "end": v(31.52, -11.77) * mm});
            skLineSegment(sketch, "E406", {"start": v(31.52, -11.77) * mm, "end": v(31.06, -11.94) * mm});
            skLineSegment(sketch, "E407", {"start": v(31.06, -11.94) * mm, "end": v(30.6, -12.1) * mm});
            skLineSegment(sketch, "E408", {"start": v(30.6, -12.1) * mm, "end": v(30.12, -12.24) * mm});
            skLineSegment(sketch, "E409", {"start": v(30.12, -12.24) * mm, "end": v(29.63, -12.35) * mm});
            skLineSegment(sketch, "E410", {"start": v(29.63, -12.35) * mm, "end": v(29.14, -12.43) * mm});
            skLineSegment(sketch, "E411", {"start": v(29.14, -12.43) * mm, "end": v(28.64, -12.48) * mm});
            skLineSegment(sketch, "E412", {"start": v(28.64, -12.48) * mm, "end": v(28.14, -12.5) * mm});
            skLineSegment(sketch, "E413", {"start": v(28.14, -12.5) * mm, "end": v(27.78, -12.5) * mm});
            skLineSegment(sketch, "E414", {"start": v(27.78, -12.5) * mm, "end": v(27.43, -12.47) * mm});
            skLineSegment(sketch, "E415", {"start": v(27.43, -12.47) * mm, "end": v(27.09, -12.44) * mm});
            skLineSegment(sketch, "E416", {"start": v(27.09, -12.44) * mm, "end": v(26.76, -12.4) * mm});
            skLineSegment(sketch, "E417", {"start": v(26.76, -12.4) * mm, "end": v(26.45, -12.34) * mm});
            skLineSegment(sketch, "E418", {"start": v(26.45, -12.34) * mm, "end": v(26.14, -12.27) * mm});
            skLineSegment(sketch, "E419", {"start": v(26.14, -12.27) * mm, "end": v(25.85, -12.18) * mm});
            skLineSegment(sketch, "E420", {"start": v(25.85, -12.18) * mm, "end": v(25.57, -12.08) * mm});
            skLineSegment(sketch, "E421", {"start": v(25.57, -12.08) * mm, "end": v(25.3, -11.97) * mm});
            skLineSegment(sketch, "E422", {"start": v(25.3, -11.97) * mm, "end": v(25.05, -11.85) * mm});
            skLineSegment(sketch, "E423", {"start": v(25.05, -11.85) * mm, "end": v(24.8, -11.7) * mm});
            skLineSegment(sketch, "E424", {"start": v(24.8, -11.7) * mm, "end": v(24.57, -11.56) * mm});
            skLineSegment(sketch, "E425", {"start": v(24.57, -11.56) * mm, "end": v(24.35, -11.4) * mm});
            skLineSegment(sketch, "E426", {"start": v(24.35, -11.4) * mm, "end": v(24.14, -11.24) * mm});
            skLineSegment(sketch, "E427", {"start": v(24.14, -11.24) * mm, "end": v(23.94, -11.06) * mm});
            skLineSegment(sketch, "E428", {"start": v(23.94, -11.06) * mm, "end": v(23.75, -10.87) * mm});
            skLineSegment(sketch, "E429", {"start": v(23.75, -10.87) * mm, "end": v(23.58, -10.67) * mm});
            skLineSegment(sketch, "E430", {"start": v(23.58, -10.67) * mm, "end": v(23.41, -10.46) * mm});
            skLineSegment(sketch, "E431", {"start": v(23.41, -10.46) * mm, "end": v(23.26, -10.23) * mm});
            skLineSegment(sketch, "E432", {"start": v(23.26, -10.23) * mm, "end": v(23.11, -10) * mm});
            skLineSegment(sketch, "E433", {"start": v(23.11, -10) * mm, "end": v(22.98, -9.76) * mm});
            skLineSegment(sketch, "E434", {"start": v(22.98, -9.76) * mm, "end": v(22.86, -9.5) * mm});
            skLineSegment(sketch, "E435", {"start": v(22.86, -9.5) * mm, "end": v(22.76, -9.24) * mm});
            skLineSegment(sketch, "E436", {"start": v(22.76, -9.24) * mm, "end": v(22.66, -8.96) * mm});
            skLineSegment(sketch, "E437", {"start": v(22.66, -8.96) * mm, "end": v(22.57, -8.67) * mm});
            skLineSegment(sketch, "E438", {"start": v(22.57, -8.67) * mm, "end": v(22.5, -8.38) * mm});
            skLineSegment(sketch, "E439", {"start": v(22.5, -8.38) * mm, "end": v(22.44, -8.08) * mm});
            skLineSegment(sketch, "E440", {"start": v(22.44, -8.08) * mm, "end": v(22.39, -7.76) * mm});
            skLineSegment(sketch, "E441", {"start": v(22.39, -7.76) * mm, "end": v(22.35, -7.44) * mm});
            skLineSegment(sketch, "E442", {"start": v(22.35, -7.44) * mm, "end": v(22.3, -6.77) * mm});
            skLineSegment(sketch, "E443", {"start": v(22.3, -6.77) * mm, "end": v(22.3, -6.43) * mm});
            skLineSegment(sketch, "E444", {"start": v(22.3, -6.43) * mm, "end": v(22.32, -5.66) * mm});
            skLineSegment(sketch, "E445", {"start": v(22.32, -5.66) * mm, "end": v(22.38, -4.92) * mm});
            skLineSegment(sketch, "E446", {"start": v(22.38, -4.92) * mm, "end": v(22.5, -4.19) * mm});
            skLineSegment(sketch, "E447", {"start": v(22.5, -4.19) * mm, "end": v(22.64, -3.48) * mm});
            skLineSegment(sketch, "E448", {"start": v(22.64, -3.48) * mm, "end": v(22.83, -2.78) * mm});
            skLineSegment(sketch, "E449", {"start": v(22.83, -2.78) * mm, "end": v(23.06, -2.1) * mm});
            skLineSegment(sketch, "E450", {"start": v(23.06, -2.1) * mm, "end": v(23.32, -1.46) * mm});
            skLineSegment(sketch, "E451", {"start": v(23.32, -1.46) * mm, "end": v(23.61, -0.84) * mm});
            skLineSegment(sketch, "E452", {"start": v(23.61, -0.84) * mm, "end": v(23.94, -0.24) * mm});
            skLineSegment(sketch, "E453", {"start": v(23.94, -0.24) * mm, "end": v(24.3, 0.33) * mm});
            skLineSegment(sketch, "E454", {"start": v(24.3, 0.33) * mm, "end": v(24.69, 0.87) * mm});
            skLineSegment(sketch, "E455", {"start": v(24.69, 0.87) * mm, "end": v(25.1, 1.38) * mm});
            skLineSegment(sketch, "E456", {"start": v(25.1, 1.38) * mm, "end": v(25.55, 1.86) * mm});
            skLineSegment(sketch, "E457", {"start": v(25.55, 1.86) * mm, "end": v(26, 2.31) * mm});
            skLineSegment(sketch, "E458", {"start": v(26, 2.31) * mm, "end": v(26.48, 2.72) * mm});
            skLineSegment(sketch, "E459", {"start": v(26.48, 2.72) * mm, "end": v(26.98, 3.1) * mm});
            skLineSegment(sketch, "E460", {"start": v(26.98, 3.1) * mm, "end": v(27.5, 3.43) * mm});
            skLineSegment(sketch, "E461", {"start": v(27.5, 3.43) * mm, "end": v(28.03, 3.73) * mm});
            skLineSegment(sketch, "E462", {"start": v(28.03, 3.73) * mm, "end": v(28.57, 3.98) * mm});
            skLineSegment(sketch, "E463", {"start": v(28.57, 3.98) * mm, "end": v(29.13, 4.19) * mm});
            skLineSegment(sketch, "E464", {"start": v(29.13, 4.19) * mm, "end": v(29.7, 4.36) * mm});
            skLineSegment(sketch, "E465", {"start": v(29.7, 4.36) * mm, "end": v(30.28, 4.49) * mm});
            skLineSegment(sketch, "E466", {"start": v(30.28, 4.49) * mm, "end": v(30.87, 4.56) * mm});
            skLineSegment(sketch, "E467", {"start": v(30.87, 4.56) * mm, "end": v(31.46, 4.59) * mm});
            skLineSegment(sketch, "E468", {"start": v(31.46, 4.59) * mm, "end": v(32, 4.57) * mm});
            skLineSegment(sketch, "E469", {"start": v(32, 4.57) * mm, "end": v(32.25, 4.55) * mm});
            skLineSegment(sketch, "E470", {"start": v(32.25, 4.55) * mm, "end": v(32.5, 4.52) * mm});
            skLineSegment(sketch, "E471", {"start": v(32.5, 4.52) * mm, "end": v(32.75, 4.48) * mm});
            skLineSegment(sketch, "E472", {"start": v(32.75, 4.48) * mm, "end": v(32.98, 4.43) * mm});
            skLineSegment(sketch, "E473", {"start": v(32.98, 4.43) * mm, "end": v(33.21, 4.38) * mm});
            skLineSegment(sketch, "E474", {"start": v(33.21, 4.38) * mm, "end": v(33.43, 4.31) * mm});
            skLineSegment(sketch, "E475", {"start": v(33.43, 4.31) * mm, "end": v(33.65, 4.24) * mm});
            skLineSegment(sketch, "E476", {"start": v(33.65, 4.24) * mm, "end": v(33.86, 4.17) * mm});
            skLineSegment(sketch, "E477", {"start": v(33.86, 4.17) * mm, "end": v(34.06, 4.08) * mm});
            skLineSegment(sketch, "E478", {"start": v(34.06, 4.08) * mm, "end": v(34.25, 4) * mm});
            skLineSegment(sketch, "E479", {"start": v(34.25, 4) * mm, "end": v(34.43, 3.9) * mm});
            skLineSegment(sketch, "E480", {"start": v(34.43, 3.9) * mm, "end": v(34.6, 3.8) * mm});
            skLineSegment(sketch, "E481", {"start": v(34.6, 3.8) * mm, "end": v(34.77, 3.68) * mm});
            skLineSegment(sketch, "E482", {"start": v(34.77, 3.68) * mm, "end": v(34.92, 3.57) * mm});
            skLineSegment(sketch, "E483", {"start": v(34.92, 3.57) * mm, "end": v(35.07, 3.45) * mm});
            skLineSegment(sketch, "E484", {"start": v(35.07, 3.45) * mm, "end": v(35.21, 3.32) * mm});
            skLineSegment(sketch, "E485", {"start": v(35.21, 3.32) * mm, "end": v(35.34, 3.19) * mm});
            skLineSegment(sketch, "E486", {"start": v(35.34, 3.19) * mm, "end": v(35.46, 3.05) * mm});
            skLineSegment(sketch, "E487", {"start": v(35.46, 3.05) * mm, "end": v(35.57, 2.9) * mm});
            skLineSegment(sketch, "E488", {"start": v(35.57, 2.9) * mm, "end": v(35.67, 2.76) * mm});
            skLineSegment(sketch, "E489", {"start": v(35.67, 2.76) * mm, "end": v(35.76, 2.6) * mm});
            skLineSegment(sketch, "E490", {"start": v(35.76, 2.6) * mm, "end": v(35.84, 2.44) * mm});
            skLineSegment(sketch, "E491", {"start": v(35.84, 2.44) * mm, "end": v(35.92, 2.28) * mm});
            skLineSegment(sketch, "E492", {"start": v(35.92, 2.28) * mm, "end": v(35.99, 2.1) * mm});
            skLineSegment(sketch, "E493", {"start": v(35.99, 2.1) * mm, "end": v(36.05, 1.94) * mm});
            skLineSegment(sketch, "E494", {"start": v(36.05, 1.94) * mm, "end": v(36.1, 1.77) * mm});
            skLineSegment(sketch, "E495", {"start": v(36.1, 1.77) * mm, "end": v(36.13, 1.59) * mm});
            skLineSegment(sketch, "E496", {"start": v(36.13, 1.59) * mm, "end": v(36.15, 1.4) * mm});
            skLineSegment(sketch, "E497", {"start": v(36.15, 1.4) * mm, "end": v(36.17, 1.22) * mm});
            skLineSegment(sketch, "E498", {"start": v(36.17, 1.22) * mm, "end": v(36.17, 1.03) * mm});
            skLineSegment(sketch, "E499", {"start": v(25.57, -3.9) * mm, "end": v(26.5, -3.8) * mm});
            skLineSegment(sketch, "E500", {"start": v(26.5, -3.8) * mm, "end": v(27.35, -3.68) * mm});
            skLineSegment(sketch, "E501", {"start": v(27.35, -3.68) * mm, "end": v(28.15, -3.51) * mm});
            skLineSegment(sketch, "E502", {"start": v(28.15, -3.51) * mm, "end": v(28.52, -3.41) * mm});
            skLineSegment(sketch, "E503", {"start": v(28.52, -3.41) * mm, "end": v(28.89, -3.3) * mm});
            skLineSegment(sketch, "E504", {"start": v(28.89, -3.3) * mm, "end": v(29.24, -3.18) * mm});
            skLineSegment(sketch, "E505", {"start": v(29.24, -3.18) * mm, "end": v(29.57, -3.06) * mm});
            skLineSegment(sketch, "E506", {"start": v(29.57, -3.06) * mm, "end": v(29.89, -2.93) * mm});
            skLineSegment(sketch, "E507", {"start": v(29.89, -2.93) * mm, "end": v(30.19, -2.79) * mm});
            skLineSegment(sketch, "E508", {"start": v(30.19, -2.79) * mm, "end": v(30.48, -2.64) * mm});
            skLineSegment(sketch, "E509", {"start": v(30.48, -2.64) * mm, "end": v(30.75, -2.5) * mm});
            skLineSegment(sketch, "E510", {"start": v(30.75, -2.5) * mm, "end": v(31, -2.34) * mm});
            skLineSegment(sketch, "E511", {"start": v(31, -2.34) * mm, "end": v(31.25, -2.18) * mm});
            skLineSegment(sketch, "E512", {"start": v(31.25, -2.18) * mm, "end": v(31.48, -2) * mm});
            skLineSegment(sketch, "E513", {"start": v(31.48, -2) * mm, "end": v(31.7, -1.83) * mm});
            skLineSegment(sketch, "E514", {"start": v(31.7, -1.83) * mm, "end": v(31.9, -1.65) * mm});
            skLineSegment(sketch, "E515", {"start": v(31.9, -1.65) * mm, "end": v(32.08, -1.47) * mm});
            skLineSegment(sketch, "E516", {"start": v(32.08, -1.47) * mm, "end": v(32.25, -1.28) * mm});
            skLineSegment(sketch, "E517", {"start": v(32.25, -1.28) * mm, "end": v(32.4, -1.08) * mm});
            skLineSegment(sketch, "E518", {"start": v(32.4, -1.08) * mm, "end": v(32.54, -0.89) * mm});
            skLineSegment(sketch, "E519", {"start": v(32.54, -0.89) * mm, "end": v(32.67, -0.69) * mm});
            skLineSegment(sketch, "E520", {"start": v(32.67, -0.69) * mm, "end": v(32.78, -0.48) * mm});
            skLineSegment(sketch, "E521", {"start": v(32.78, -0.48) * mm, "end": v(32.87, -0.27) * mm});
            skLineSegment(sketch, "E522", {"start": v(32.87, -0.27) * mm, "end": v(32.96, -0.05) * mm});
            skLineSegment(sketch, "E523", {"start": v(32.96, -0.05) * mm, "end": v(33.02, 0.16) * mm});
            skLineSegment(sketch, "E524", {"start": v(33.02, 0.16) * mm, "end": v(33.07, 0.38) * mm});
            skLineSegment(sketch, "E525", {"start": v(33.07, 0.38) * mm, "end": v(33.1, 0.6) * mm});
            skLineSegment(sketch, "E526", {"start": v(33.1, 0.6) * mm, "end": v(33.13, 0.81) * mm});
            skLineSegment(sketch, "E527", {"start": v(33.13, 0.81) * mm, "end": v(33.14, 1.03) * mm});
            skLineSegment(sketch, "E528", {"start": v(33.14, 1.03) * mm, "end": v(33.13, 1.27) * mm});
            skLineSegment(sketch, "E529", {"start": v(33.13, 1.27) * mm, "end": v(33.12, 1.38) * mm});
            skLineSegment(sketch, "E530", {"start": v(33.12, 1.38) * mm, "end": v(33.1, 1.5) * mm});
            skLineSegment(sketch, "E531", {"start": v(33.1, 1.5) * mm, "end": v(33.09, 1.6) * mm});
            skLineSegment(sketch, "E532", {"start": v(33.09, 1.6) * mm, "end": v(33.06, 1.71) * mm});
            skLineSegment(sketch, "E533", {"start": v(33.06, 1.71) * mm, "end": v(33.04, 1.82) * mm});
            skLineSegment(sketch, "E534", {"start": v(33.04, 1.82) * mm, "end": v(33, 1.92) * mm});
            skLineSegment(sketch, "E535", {"start": v(33, 1.92) * mm, "end": v(32.97, 2.02) * mm});
            skLineSegment(sketch, "E536", {"start": v(32.97, 2.02) * mm, "end": v(32.93, 2.11) * mm});
            skLineSegment(sketch, "E537", {"start": v(32.93, 2.11) * mm, "end": v(32.88, 2.2) * mm});
            skLineSegment(sketch, "E538", {"start": v(32.88, 2.2) * mm, "end": v(32.84, 2.3) * mm});
            skLineSegment(sketch, "E539", {"start": v(32.84, 2.3) * mm, "end": v(32.78, 2.38) * mm});
            skLineSegment(sketch, "E540", {"start": v(32.78, 2.38) * mm, "end": v(32.73, 2.47) * mm});
            skLineSegment(sketch, "E541", {"start": v(32.73, 2.47) * mm, "end": v(32.67, 2.55) * mm});
            skLineSegment(sketch, "E542", {"start": v(32.67, 2.55) * mm, "end": v(32.6, 2.63) * mm});
            skLineSegment(sketch, "E543", {"start": v(32.6, 2.63) * mm, "end": v(32.53, 2.7) * mm});
            skLineSegment(sketch, "E544", {"start": v(32.53, 2.7) * mm, "end": v(32.46, 2.77) * mm});
            skLineSegment(sketch, "E545", {"start": v(32.46, 2.77) * mm, "end": v(32.39, 2.84) * mm});
            skLineSegment(sketch, "E546", {"start": v(32.39, 2.84) * mm, "end": v(32.3, 2.9) * mm});
            skLineSegment(sketch, "E547", {"start": v(32.3, 2.9) * mm, "end": v(32.23, 2.96) * mm});
            skLineSegment(sketch, "E548", {"start": v(32.23, 2.96) * mm, "end": v(32.14, 3) * mm});
            skLineSegment(sketch, "E549", {"start": v(32.14, 3) * mm, "end": v(32.05, 3.06) * mm});
            skLineSegment(sketch, "E550", {"start": v(32.05, 3.06) * mm, "end": v(31.96, 3.1) * mm});
            skLineSegment(sketch, "E551", {"start": v(31.96, 3.1) * mm, "end": v(31.86, 3.13) * mm});
            skLineSegment(sketch, "E552", {"start": v(31.86, 3.13) * mm, "end": v(31.76, 3.17) * mm});
            skLineSegment(sketch, "E553", {"start": v(31.76, 3.17) * mm, "end": v(31.65, 3.2) * mm});
            skLineSegment(sketch, "E554", {"start": v(31.65, 3.2) * mm, "end": v(31.55, 3.21) * mm});
            skLineSegment(sketch, "E555", {"start": v(31.55, 3.21) * mm, "end": v(31.43, 3.23) * mm});
            skLineSegment(sketch, "E556", {"start": v(31.43, 3.23) * mm, "end": v(31.32, 3.24) * mm});
            skLineSegment(sketch, "E557", {"start": v(31.32, 3.24) * mm, "end": v(31.2, 3.25) * mm});
            skLineSegment(sketch, "E558", {"start": v(31.2, 3.25) * mm, "end": v(31.07, 3.25) * mm});
            skLineSegment(sketch, "E559", {"start": v(31.07, 3.25) * mm, "end": v(30.82, 3.24) * mm});
            skLineSegment(sketch, "E560", {"start": v(30.82, 3.24) * mm, "end": v(30.57, 3.21) * mm});
            skLineSegment(sketch, "E561", {"start": v(30.57, 3.21) * mm, "end": v(30.32, 3.16) * mm});
            skLineSegment(sketch, "E562", {"start": v(30.32, 3.16) * mm, "end": v(30.08, 3.09) * mm});
            skLineSegment(sketch, "E563", {"start": v(30.08, 3.09) * mm, "end": v(29.84, 3) * mm});
            skLineSegment(sketch, "E564", {"start": v(29.84, 3) * mm, "end": v(29.6, 2.88) * mm});
            skLineSegment(sketch, "E565", {"start": v(29.6, 2.88) * mm, "end": v(29.38, 2.75) * mm});
            skLineSegment(sketch, "E566", {"start": v(29.38, 2.75) * mm, "end": v(29.15, 2.6) * mm});
            skLineSegment(sketch, "E567", {"start": v(29.15, 2.6) * mm, "end": v(28.92, 2.43) * mm});
            skLineSegment(sketch, "E568", {"start": v(28.92, 2.43) * mm, "end": v(28.7, 2.25) * mm});
            skLineSegment(sketch, "E569", {"start": v(28.7, 2.25) * mm, "end": v(28.5, 2.06) * mm});
            skLineSegment(sketch, "E570", {"start": v(28.5, 2.06) * mm, "end": v(28.29, 1.86) * mm});
            skLineSegment(sketch, "E571", {"start": v(28.29, 1.86) * mm, "end": v(28.09, 1.64) * mm});
            skLineSegment(sketch, "E572", {"start": v(28.09, 1.64) * mm, "end": v(27.7, 1.18) * mm});
            skLineSegment(sketch, "E573", {"start": v(27.7, 1.18) * mm, "end": v(27.52, 0.93) * mm});
            skLineSegment(sketch, "E574", {"start": v(27.52, 0.93) * mm, "end": v(27.17, 0.4) * mm});
            skLineSegment(sketch, "E575", {"start": v(27.17, 0.4) * mm, "end": v(26.86, -0.16) * mm});
            skLineSegment(sketch, "E576", {"start": v(26.86, -0.16) * mm, "end": v(26.57, -0.75) * mm});
            skLineSegment(sketch, "E577", {"start": v(26.57, -0.75) * mm, "end": v(26.3, -1.38) * mm});
            skLineSegment(sketch, "E578", {"start": v(26.3, -1.38) * mm, "end": v(26.07, -2.01) * mm});
            skLineSegment(sketch, "E579", {"start": v(26.07, -2.01) * mm, "end": v(25.87, -2.64) * mm});
            skLineSegment(sketch, "E580", {"start": v(25.87, -2.64) * mm, "end": v(25.7, -3.27) * mm});
            skLineSegment(sketch, "E581", {"start": v(25.7, -3.27) * mm, "end": v(25.57, -3.9) * mm});
            skSolve(sketch);
        }
        {
            var Q0;
            Q0=makeQuery(id+"F0.imprint","IMPRINT",FACE,{"disambiguationData":[TD([[makeQuery(id+"F0.imprint","IMPRINT",EDGE,{"derivedFrom":sQuery(id+"F0.wireOp",EDGE,"9c274906-66f2-47cc-ba81-bc829715841a")}),-1.0]])]});
            var Q1;
            {var subQ1=sQuery(id+"F0.wireOp",EDGE,"E3");Q1=makeQuery(id+"F0.imprint","IMPRINT",FACE,{"disambiguationData":[TD([[makeQuery(id+"F0.imprint","IMPRINT",EDGE,{"derivedFrom":subQ1}),-1.0]])]});}
            var Q2;
            Q2=makeQuery(id+"F0.imprint","IMPRINT",FACE,{"disambiguationData":[TD([[makeQuery(id+"F0.imprint","IMPRINT",EDGE,{"derivedFrom":sQuery(id+"F0.wireOp",EDGE,"6ab65d4b-20cc-4260-84e2-1f812e6f8199")}),1.0]])]});
            var Q3;
            Q3=makeQuery(id+"F0.imprint","IMPRINT",FACE,{"disambiguationData":[TD([[makeQuery(id+"F0.imprint","IMPRINT",EDGE,{"derivedFrom":sQuery(id+"F0.wireOp",EDGE,"fbc92326-29e4-4a65-8bcc-6a279c66f74b")}),-1.0]])]});
            var Q4;
            Q4=makeQuery(id+"F0.imprint","IMPRINT",FACE,{"disambiguationData":[TD([[makeQuery(id+"F0.imprint","IMPRINT",EDGE,{"derivedFrom":sQuery(id+"F0.wireOp",EDGE,"E1")}),1.0]])]});
            var Q5;
            Q5=makeQuery(id+"F0.imprint","IMPRINT",FACE,{"disambiguationData":[TD([[makeQuery(id+"F0.imprint","IMPRINT",EDGE,{"derivedFrom":sQuery(id+"F0.wireOp",EDGE,"edff43eb-599a-4c31-8809-e4d85603c349")}),-1.0]])]});
            var Q6;
            Q6=makeQuery(id+"F0.imprint","IMPRINT",FACE,{"disambiguationData":[TD([[makeQuery(id+"F0.imprint","IMPRINT",EDGE,{"derivedFrom":sQuery(id+"F0.wireOp",EDGE,"9c1aa12f-a708-4583-be26-2b383a722471")}),1.0]])]});
            var Q7;
            Q7=makeQuery(id+"F0.imprint","IMPRINT",FACE,{"disambiguationData":[TD([[makeQuery(id+"F0.imprint","IMPRINT",EDGE,{"derivedFrom":sQuery(id+"F0.wireOp",EDGE,"d64aa239-00f7-4386-9746-6503c5a989f5")}),-1.0]])]});
            var Q8;
            {var subQ5=sQuery(id+"F0.wireOp",EDGE,"E6");Q8=makeQuery(id+"F0.imprint","IMPRINT",FACE,{"disambiguationData":[TD([[makeQuery(id+"F0.imprint","IMPRINT",EDGE,{"derivedFrom":subQ5}),-1.0]])]});}
            var Q9;
            Q9=makeQuery(id+"F0.imprint","IMPRINT",FACE,{"disambiguationData":[TD([[makeQuery(id+"F0.imprint","IMPRINT",EDGE,{"derivedFrom":sQuery(id+"F0.wireOp",EDGE,"E61")}),-1.0]])]});
            var Q10;
            Q10=makeQuery(id+"F0.imprint","IMPRINT",FACE,{"disambiguationData":[TD([[makeQuery(id+"F0.imprint","IMPRINT",EDGE,{"derivedFrom":sQuery(id+"F0.wireOp",EDGE,"E294")}),-1.0]])]});
            var Q11;
            Q11=makeQuery(id+"F0.imprint","IMPRINT",FACE,{"disambiguationData":[TD([[makeQuery(id+"F0.imprint","IMPRINT",EDGE,{"derivedFrom":sQuery(id+"F0.wireOp",EDGE,"E314")}),-1.0]])]});
            var Q12;
            Q12=makeQuery(id+"F0.imprint","IMPRINT",FACE,{"disambiguationData":[TD([[makeQuery(id+"F0.imprint","IMPRINT",EDGE,{"derivedFrom":sQuery(id+"F0.wireOp",EDGE,"E61")}),1.0]])]});
            var Q13;
            Q13=makeQuery(id+"F0.imprint","IMPRINT",FACE,{"disambiguationData":[TD([[makeQuery(id+"F0.imprint","IMPRINT",EDGE,{"derivedFrom":sQuery(id+"F0.wireOp",EDGE,"E499")}),1.0]])]});
            extrude(context, id + "F1", {"entities" : qUnion([Q0, Q1, Q2, Q3, Q4, Q5, Q6, Q7, Q8, Q9, Q10, Q11, Q12, Q13]), "oppositeDirection" : true, "depth" : 1.6 * mm, "offsetDistance" : 25 * mm});
        }
        {
            var Q0;
            Q0=makeQuery(id+"F0.imprint","IMPRINT",FACE,{"disambiguationData":[TD([[makeQuery(id+"F0.imprint","IMPRINT",EDGE,{"derivedFrom":sQuery(id+"F0.wireOp",EDGE,"E1")}),1.0]])]});
            extrude(context, id + "F2", {"entities" : qUnion([Q0]), "operationType" : NewBodyOperationType.ADD, "depth" : 1.6 * mm, "offsetDistance" : 25 * mm});
        }
        {
            var Q0;
            Q0=makeQuery(id+"F0.imprint","IMPRINT",FACE,{"disambiguationData":[TD([[makeQuery(id+"F0.imprint","IMPRINT",EDGE,{"derivedFrom":sQuery(id+"F0.wireOp",EDGE,"E61")}),-1.0]])]});
            var Q1;
            Q1=makeQuery(id+"F0.imprint","IMPRINT",FACE,{"disambiguationData":[TD([[makeQuery(id+"F0.imprint","IMPRINT",EDGE,{"derivedFrom":sQuery(id+"F0.wireOp",EDGE,"E294")}),-1.0]])]});
            var Q2;
            Q2=makeQuery(id+"F0.imprint","IMPRINT",FACE,{"disambiguationData":[TD([[makeQuery(id+"F0.imprint","IMPRINT",EDGE,{"derivedFrom":sQuery(id+"F0.wireOp",EDGE,"E314")}),-1.0]])]});
            var Q3;
            {var subQ5=sQuery(id+"F0.wireOp",EDGE,"E6");Q3=makeQuery(id+"F0.imprint","IMPRINT",FACE,{"disambiguationData":[TD([[makeQuery(id+"F0.imprint","IMPRINT",EDGE,{"derivedFrom":subQ5}),-1.0]])]});}
            extrude(context, id + "F3", {"entities" : qUnion([Q0, Q1, Q2, Q3]), "operationType" : NewBodyOperationType.ADD, "depth" : 1 * mm, "offsetDistance" : 25 * mm});
        }
    });
